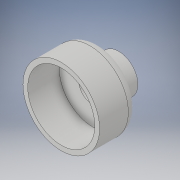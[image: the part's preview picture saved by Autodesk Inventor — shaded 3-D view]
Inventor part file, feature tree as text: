
AUTODESK INVENTOR PART (.ipt)
format: ipt  version: 2019 (Build 230136000, 136)  size: 137,216 bytes
history: native  units: mm
features: extrude x4, sketch x3, fillet x1
ambient origin geometry x8: Origin, YZ Plane, XZ Plane, XY Plane, X Axis, Y Axis, Z Axis, Center Point
bodies: Solid1 (feature_tree)
feature tree (8):
  sketch  "Sketch1"  dims[d0=80.0mm d1=30.0mm]
  extrude  "Extrusion1"  Depth=30.0mm
  extrude  "Extrusion2"  Depth=40.0mm
  extrude  "Extrusion3"  Depth=20.0mm TaperAngle=0.0deg
  fillet  "Fillet1"  Radius=10.0mm
  extrude  "Extrusion4"  Depth=33.0mm
  sketch  "Sketch2"  dims[d2=40.0mm d3=0.0mm d4=40.0mm]
  sketch  "Sketch3"  dims[d5=20.0mm d6=0.0mm d7=20.0mm d8=0.0mm d9=10.0mm d10=70.0mm d11=33.0mm d12=0.0mm]
